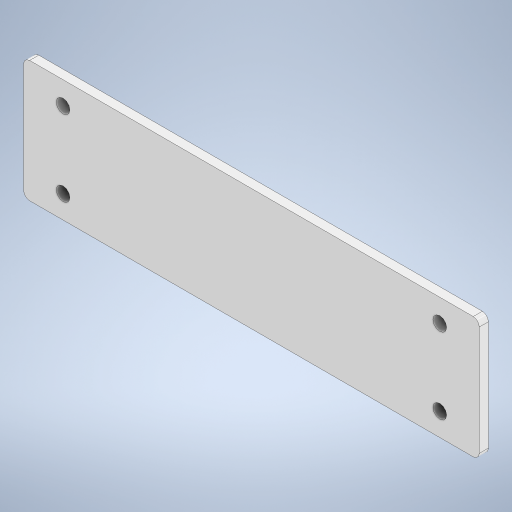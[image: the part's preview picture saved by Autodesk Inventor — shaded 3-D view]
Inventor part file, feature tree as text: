
AUTODESK INVENTOR PART (.ipt)
format: ipt  version: 2024 (Build 280153000, 153)  size: 234,496 bytes
history: native  units: mm
features: extrude x2, sketch x2, fillet x1
ambient origin geometry x8: Origin, YZ Plane, XZ Plane, XY Plane, X Axis, Y Axis, Z Axis, Center Point
bodies: Volumenkörper1 (feature_tree)
feature tree (5):
  extrude  "Extrusion1"  Depth=150.0mm
  extrude  "Extrusion2"  Depth=2.0mm
  fillet  "Rundung1"  Radius=4.5mm
  sketch  "Skizze1"  dims[d0=40.0mm d1=150.0mm]
  sketch  "Skizze2"  dims[d2=3.0mm d3=0.0mm d4=13.0mm d5=4.5mm d6=4.5mm d7=25.0mm d8=3.0mm d9=0.0mm d10=2.0mm]
